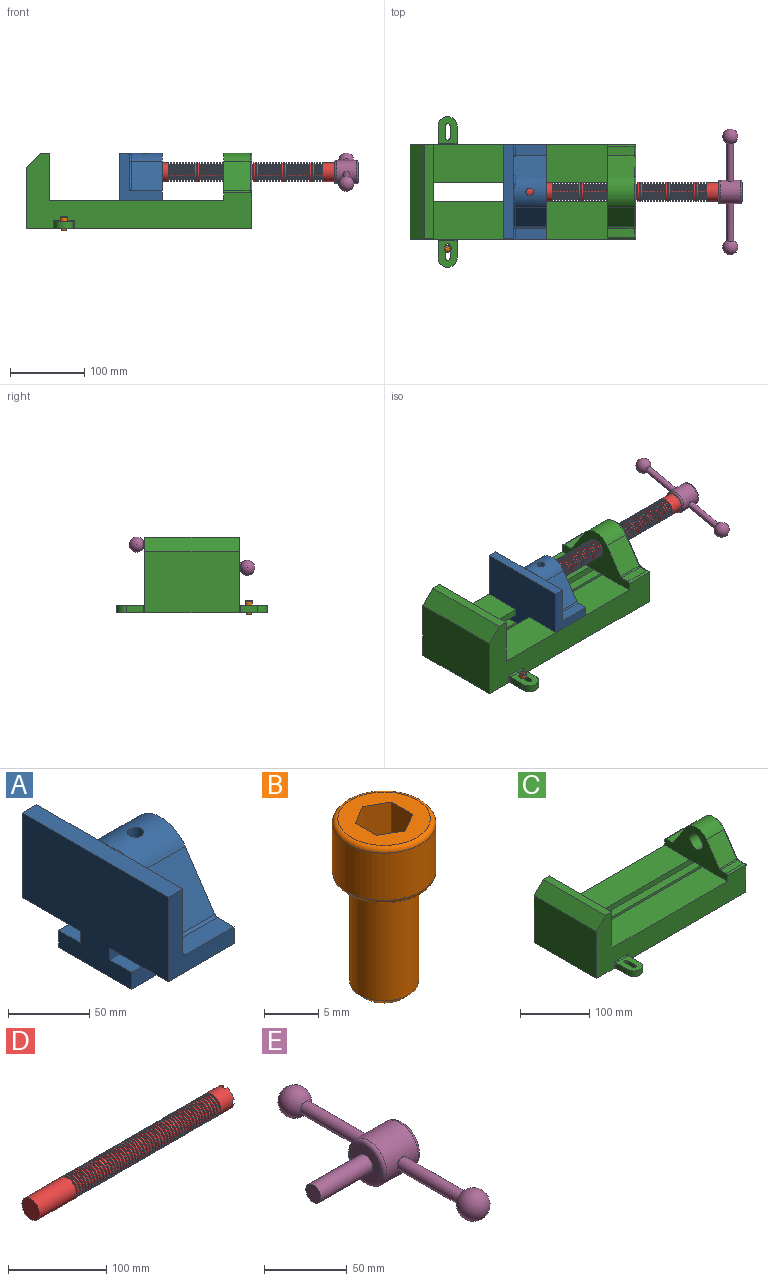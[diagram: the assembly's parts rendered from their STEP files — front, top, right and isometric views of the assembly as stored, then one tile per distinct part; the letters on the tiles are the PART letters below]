
ASSEMBLY  parts=5 mates=5
PART A: 36 faces, bbox 57.2x127x89 mm
  f0: plane 57.15x50.8mm, normal (0,0,-1), area 2903.2mm2, adj f6,f9,f10,f23
  f1: cylinder r=12.7mm len=44.45mm, axis (1,0,0), area 3464.3mm2, adj f6,f15,f16
  f2: plane 41.91x14.52mm, normal (0,0,1), area 608.5mm2, adj f6,f11,f24,f25
  f3: plane 51.86x48.26mm, normal (1,0,0), area 1495.7mm2, adj f8,f10,f31,f33,f35
  f4: plane 51.86x48.26mm, normal (1,0,0), area 1495.7mm2, adj f8,f11,f24,f28,f29
  f5: plane 57.15x50.8mm, normal (0,0,-1), area 2903.2mm2, adj f6,f9,f11,f22
  f6: plane 127x85.09mm, normal (1,0,0), area 5190.6mm2, adj f0,f1,f2,f5,f7,f10,f11,f12
  f7: plane 41.91x14.52mm, normal (0,0,1), area 608.5mm2, adj f6,f10,f30,f31
  f8: plane 127x12.7mm, normal (0,0,1), area 1612.9mm2, adj f3,f4,f9,f10,f11,f26,f34
  f9: plane 127x85.09mm, normal (-1,0,0), area 9096.8mm2, adj f0,f5,f8,f10,f11,f17,f18,f19
  f10: plane 63.5x57.15mm, normal (0,-1,0), area 1372.3mm2, adj f0,f3,f6,f7,f8,f9,f31
  f11: plane 63.5x57.15mm, normal (0,1,0), area 1372.3mm2, adj f2,f4,f5,f6,f8,f9,f24
  f12: plane 41.91x38.43mm, normal (0,-0.83,0.56), area 1939.2mm2, adj f6,f13,f30,f33
  f13: cylinder r=25.4mm len=44.45mm, axis (1,0,0), area 2026.5mm2, adj f6,f12,f14,f16,f26,f28,f34,f35
  f14: plane 41.91x38.43mm, normal (0,0.83,0.56), area 1939.2mm2, adj f6,f13,f25,f29
  f15: plane 25.4x25.4mm, normal (1,0,0), area 506.7mm2, adj f1
  f16: cylinder r=5.08mm len=13.76mm, axis (0,0,1), area 414mm2, adj f1,f13
  f17: plane 57.15x19.05mm, normal (0,0,1), area 1088.7mm2, adj f6,f9,f18,f23
  f18: plane 57.15x12.7mm, normal (0,-1,0), area 725.8mm2, adj f6,f9,f17,f19
  f19: plane 63.5x57.15mm, normal (0,0,-1), area 3629mm2, adj f6,f9,f18,f20
  f20: plane 57.15x12.7mm, normal (0,1,0), area 725.8mm2, adj f6,f9,f19,f21
  f21: plane 57.15x19.05mm, normal (0,0,1), area 1088.7mm2, adj f6,f9,f20,f22
  f22: plane 57.15x8.89mm, normal (0,1,0), area 508.1mm2, adj f5,f6,f9,f21
  f23: plane 57.15x8.89mm, normal (0,-1,0), area 508.1mm2, adj f0,f6,f9,f17
  f24: cylinder r=2.54mm len=14.52mm, axis (0,-1,0), area 57.9mm2, adj f2,f4,f11,f27
  f25: cylinder r=2.54mm len=41.91mm, axis (1,0,0), area 104.3mm2, adj f2,f6,f14,f27
  f26: bspline ~12.24x2.8mm, area 20.9mm2, adj f8,f13,f28
  f27: sphere r=2.54mm, area 6.3mm2, adj f24,f25,f29
  f28: torus R=27.94mm, axis (1,0,0), area 57.8mm2, adj f4,f13,f26,f29
  f29: cylinder r=2.54mm len=39.84mm, axis (0,-0.56,0.83), area 184.6mm2, adj f4,f14,f27,f28
  f30: cylinder r=2.54mm len=41.91mm, axis (1,0,0), area 104.3mm2, adj f6,f7,f12,f32
  f31: cylinder r=2.54mm len=14.52mm, axis (0,-1,0), area 57.9mm2, adj f3,f7,f10,f32
  f32: sphere r=2.54mm, area 6.3mm2, adj f30,f31,f33
  f33: cylinder r=2.54mm len=39.84mm, axis (0,-0.56,-0.83), area 184.6mm2, adj f3,f12,f32,f35
  f34: bspline ~12.24x2.8mm, area 20.9mm2, adj f8,f13,f35
  f35: torus R=27.94mm, axis (1,0,0), area 57.8mm2, adj f3,f13,f33,f34
PART B: 15 faces, bbox 10.3x10.3x19.1 mm
  f0: plane 8.51x8.51mm, normal (0,0,1), area 37.2mm2, adj f5,f6,f7,f8,f9,f10,f14
  f1: cylinder r=3.17mm len=11.94mm, axis (0,0,1), area 238.2mm2, adj f4,f12
  f2: plane 4.83x4.83mm, normal (0,0,-1), area 18.3mm2, adj f12
  f3: cylinder r=4.76mm len=9.53mm, axis (0,0,-1), area 159.6mm2, adj f13,f14
  f4: plane 8.51x8.51mm, normal (0,0,-1), area 25.2mm2, adj f1,f13
  f5: plane 4.83x2.38mm, normal (-0.5,-0.87,0), area 13.3mm2, adj f0,f6,f10,f11
  f6: plane 4.83x2.38mm, normal (0.5,-0.87,0), area 13.3mm2, adj f0,f5,f7,f11
  f7: plane 4.83x2.75mm, normal (1,0,0), area 13.3mm2, adj f0,f6,f8,f11
  f8: plane 4.83x2.38mm, normal (0.5,0.87,0), area 13.3mm2, adj f0,f7,f9,f11
  f9: plane 4.83x2.38mm, normal (-0.5,0.87,0), area 13.3mm2, adj f0,f8,f10,f11
  f10: plane 4.83x2.75mm, normal (-1,0,0), area 13.3mm2, adj f0,f5,f9,f11
  f11: plane 5.5x4.76mm, normal (0,0,1), area 19.6mm2, adj f5,f6,f7,f8,f9,f10
  f12: cone r=3.17mm half-angle=45deg, axis (0,0,1), area 18.9mm2, adj f1,f2
  f13: torus R=4.25mm, axis (0,0,1), area 23mm2, adj f3,f4
  f14: torus R=4.25mm, axis (0,0,1), area 23mm2, adj f0,f3
PART C: 61 faces, bbox 304.8x203.2x103.7 mm
  f0: plane 304.8x101.6mm, normal (0,1,0), area 13520.3mm2, adj f3,f4,f5,f6,f7,f8,f9,f16
  f1: plane 304.8x101.6mm, normal (0,-1,0), area 13520.3mm2, adj f2,f3,f5,f6,f7,f8,f9,f16
  f2: plane 234.95x50.8mm, normal (0,0,1), area 11935.5mm2, adj f1,f5,f16,f26
  f3: plane 127x99.06mm, normal (1,0,0), area 7097.5mm2, adj f0,f1,f9,f14,f17,f18,f19,f20
  f4: plane 234.95x50.8mm, normal (0,0,1), area 11935.5mm2, adj f0,f5,f16,f27
  f5: plane 127x101.6mm, normal (1,0,0), area 9516.1mm2, adj f0,f1,f2,f4,f6,f9,f18,f19
  f6: plane 127x12.7mm, normal (0,0,1), area 1612.9mm2, adj f0,f1,f5,f7
  f7: plane 127x19.05mm, normal (-0.71,0,0.71), area 3421.5mm2, adj f0,f1,f6,f8
  f8: plane 127x82.55mm, normal (-1,0,0), area 10483.8mm2, adj f0,f1,f7,f9
  f9: plane 304.8x203.2mm, normal (0,0,-1), area 33298.3mm2, adj f0,f1,f3,f5,f8,f21,f22,f39
  f10: plane 35.56x11.98mm, normal (0,0,1), area 426mm2, adj f16,f28,f29,f30
  f11: plane 38.43x35.56mm, normal (0,0.83,0.56), area 1645.4mm2, adj f12,f16,f29,f32
  f12: cylinder r=25.4mm len=42.19mm, axis (1,0,0), area 1770.2mm2, adj f11,f13,f16,f33
  f13: plane 38.43x35.56mm, normal (0,-0.83,0.56), area 1645.4mm2, adj f12,f16,f34,f35
  f14: cylinder r=12.7mm len=38.1mm, axis (1,0,0), area 3040.2mm2, adj f3,f16
  f15: plane 35.56x11.98mm, normal (0,0,1), area 426mm2, adj f16,f34,f36,f38
  f16: plane 127x63.5mm, normal (-1,0,0), area 4155.5mm2, adj f0,f1,f2,f4,f10,f11,f12,f13
  f17: plane 38.1x25.4mm, normal (0,0,-1), area 967.7mm2, adj f3,f16,f26,f27
  f18: plane 273.05x19.05mm, normal (0,0,-1), area 5201.6mm2, adj f3,f5,f19,f26
  f19: plane 273.05x12.7mm, normal (0,1,0), area 3467.7mm2, adj f3,f5,f18,f20
  f20: plane 273.05x19.05mm, normal (0,0,1), area 5201.6mm2, adj f3,f5,f19,f21
  f21: plane 273.05x16.51mm, normal (0,1,0), area 4508.1mm2, adj f3,f5,f9,f20
  f22: plane 273.05x16.51mm, normal (0,-1,0), area 4508.1mm2, adj f3,f5,f9,f23
  f23: plane 273.05x19.05mm, normal (0,0,1), area 5201.6mm2, adj f3,f5,f22,f24
  f24: plane 273.05x12.7mm, normal (0,-1,0), area 3467.7mm2, adj f3,f5,f23,f25
  f25: plane 273.05x19.05mm, normal (0,0,-1), area 5201.6mm2, adj f3,f5,f24,f27
  f26: plane 273.05x8.89mm, normal (0,1,0), area 2427.4mm2, adj f2,f3,f5,f17,f18
  f27: plane 273.05x8.89mm, normal (0,-1,0), area 2427.4mm2, adj f3,f4,f5,f17,f25
  f28: cylinder r=2.54mm len=38.1mm, axis (1,0,0), area 148.3mm2, adj f0,f10,f16,f30
  f29: cylinder r=2.54mm len=35.56mm, axis (-1,0,0), area 88.5mm2, adj f10,f11,f16,f31
  f30: cylinder r=2.54mm len=14.52mm, axis (0,1,0), area 54.3mm2, adj f3,f10,f28,f31
  f31: torus R=5.08mm, axis (-1,0,0), area 13.5mm2, adj f3,f29,f30,f32
  f32: cylinder r=2.54mm len=39.84mm, axis (0,0.56,-0.83), area 184.6mm2, adj f3,f11,f31,f33
  f33: torus R=22.86mm, axis (-1,0,0), area 191.4mm2, adj f3,f12,f32,f35
  f34: cylinder r=2.54mm len=35.56mm, axis (-1,0,0), area 88.5mm2, adj f13,f15,f16,f37
  f35: cylinder r=2.54mm len=39.84mm, axis (0,0.56,0.83), area 184.6mm2, adj f3,f13,f33,f37
  f36: cylinder r=2.54mm len=38.1mm, axis (-1,0,0), area 148.3mm2, adj f1,f15,f16,f38
  f37: torus R=5.08mm, axis (-1,0,0), area 13.5mm2, adj f3,f34,f35,f38
  f38: cylinder r=2.54mm len=14.52mm, axis (0,1,0), area 54.3mm2, adj f3,f15,f36,f37
  f39: plane 23.88x9.53mm, normal (-1,0,0), area 227.4mm2, adj f9,f45,f46,f60
  f40: plane 23.88x9.53mm, normal (1,0,0), area 227.4mm2, adj f9,f45,f46,f58
  f41: cylinder r=3.3mm len=9.53mm, axis (0,0,-1), area 98.8mm2, adj f9,f42,f44,f46
  f42: plane 15.62x9.53mm, normal (-1,0,0), area 148.8mm2, adj f9,f41,f43,f46
  f43: cylinder r=3.3mm len=9.53mm, axis (0,0,-1), area 98.8mm2, adj f9,f42,f44,f46
  f44: plane 15.62x9.53mm, normal (1,0,0), area 148.8mm2, adj f9,f41,f43,f46
  f45: cylinder r=12.7mm len=25.4mm, axis (0,0,-1), area 380mm2, adj f9,f39,f40,f46
  f46: plane 36.58x25.4mm, normal (0,0,1), area 722.4mm2, adj f39,f40,f41,f42,f43,f44,f45,f59
  f47: plane 23.88x9.53mm, normal (-1,0,0), area 227.4mm2, adj f9,f53,f54,f56
  f48: plane 23.88x9.53mm, normal (1,0,0), area 227.4mm2, adj f9,f53,f54,f55
  f49: cylinder r=3.3mm len=9.53mm, axis (0,0,-1), area 98.8mm2, adj f9,f50,f52,f54
  f50: plane 15.62x9.53mm, normal (-1,0,0), area 148.8mm2, adj f9,f49,f51,f54
  f51: cylinder r=3.3mm len=9.53mm, axis (0,0,-1), area 98.8mm2, adj f9,f50,f52,f54
  f52: plane 15.62x9.53mm, normal (1,0,0), area 148.8mm2, adj f9,f49,f51,f54
  f53: cylinder r=12.7mm len=25.4mm, axis (0,0,-1), area 380mm2, adj f9,f47,f48,f54
  f54: plane 36.58x25.4mm, normal (0,0,1), area 722.4mm2, adj f47,f48,f49,f50,f51,f52,f53,f57
  f55: cylinder r=1.52mm len=11.05mm, axis (0,0,-1), area 24.1mm2, adj f0,f9,f48,f57
  f56: cylinder r=1.52mm len=11.05mm, axis (0,0,1), area 24.1mm2, adj f0,f9,f47,f57
  f57: cylinder r=1.52mm len=28.45mm, axis (1,0,0), area 63.5mm2, adj f0,f54,f55,f56
  f58: cylinder r=1.52mm len=11.05mm, axis (0,0,1), area 24.1mm2, adj f1,f9,f40,f59
  f59: cylinder r=1.52mm len=28.45mm, axis (-1,0,0), area 63.5mm2, adj f1,f46,f58,f60
  f60: cylinder r=1.52mm len=11.05mm, axis (0,0,-1), area 24.1mm2, adj f1,f9,f39,f59
PART D: 220 faces, bbox 279.4x25.4x25.4 mm
  f0: cylinder r=12.7mm len=25.4mm, axis (-1,0,0), area 1468.2mm2, adj f1,f2,f3,f5,f7,f208,f209,f210
  f1: plane 9.9x9.9mm, normal (1,0,0), area 62.3mm2, adj f0,f4,f213,f216
  f2: plane 9.9x9.9mm, normal (1,0,0), area 62.3mm2, adj f0,f4,f210,f218
  f3: plane 9.9x9.9mm, normal (1,0,0), area 62.3mm2, adj f0,f4,f209,f212
  f4: cylinder r=6.35mm len=25.4mm, axis (1,0,0), area 960.3mm2, adj f1,f2,f3,f5,f6,f208,f209,f210
  f5: plane 9.9x9.9mm, normal (1,0,0), area 62.3mm2, adj f0,f4,f215,f217
  f6: plane 12.7x12.7mm, normal (1,0,0), area 126.7mm2, adj f4
  f7: cone r=12.7mm half-angle=76deg, axis (1,0,0), area 188mm2, adj f0,f9
  f8: cone r=10.16mm half-angle=76deg, axis (-1,0,0), area 188mm2, adj f9,f10
  f9: cylinder r=10.16mm len=20.32mm, axis (1,0,0), area 81.1mm2, adj f7,f8
  f10: cylinder r=12.7mm len=25.4mm, axis (-1,0,0), area 131.7mm2, adj f8,f11
  f11: cone r=12.7mm half-angle=76deg, axis (1,0,0), area 188mm2, adj f10,f13
  f12: cone r=10.16mm half-angle=76deg, axis (-1,0,0), area 188mm2, adj f13,f14
  f13: cylinder r=10.16mm len=20.32mm, axis (1,0,0), area 81.1mm2, adj f11,f12
  f14: cylinder r=12.7mm len=25.4mm, axis (-1,0,0), area 131.7mm2, adj f12,f15
  f15: cone r=12.7mm half-angle=76deg, axis (1,0,0), area 188mm2, adj f14,f17
  f16: cone r=10.16mm half-angle=76deg, axis (-1,0,0), area 188mm2, adj f17,f18
  f17: cylinder r=10.16mm len=20.32mm, axis (1,0,0), area 81.1mm2, adj f15,f16
  f18: cylinder r=12.7mm len=25.4mm, axis (-1,0,0), area 131.7mm2, adj f16,f19
  f19: cone r=12.7mm half-angle=76deg, axis (1,0,0), area 188mm2, adj f18,f21
  f20: cone r=10.16mm half-angle=76deg, axis (-1,0,0), area 188mm2, adj f21,f22
  f21: cylinder r=10.16mm len=20.32mm, axis (1,0,0), area 81.1mm2, adj f19,f20
  f22: cylinder r=12.7mm len=25.4mm, axis (-1,0,0), area 131.7mm2, adj f20,f23
  f23: cone r=12.7mm half-angle=76deg, axis (1,0,0), area 188mm2, adj f22,f25
  f24: cone r=10.16mm half-angle=76deg, axis (-1,0,0), area 188mm2, adj f25,f26
  f25: cylinder r=10.16mm len=20.32mm, axis (1,0,0), area 81.1mm2, adj f23,f24
  f26: cylinder r=12.7mm len=25.4mm, axis (-1,0,0), area 131.7mm2, adj f24,f27
  f27: cone r=12.7mm half-angle=76deg, axis (1,0,0), area 188mm2, adj f26,f29
  f28: cone r=10.16mm half-angle=76deg, axis (-1,0,0), area 188mm2, adj f29,f30
  f29: cylinder r=10.16mm len=20.32mm, axis (1,0,0), area 81.1mm2, adj f27,f28
  f30: cylinder r=12.7mm len=25.4mm, axis (-1,0,0), area 131.7mm2, adj f28,f31
  f31: cone r=12.7mm half-angle=76deg, axis (1,0,0), area 188mm2, adj f30,f33
  f32: cone r=10.16mm half-angle=76deg, axis (-1,0,0), area 188mm2, adj f33,f34
  f33: cylinder r=10.16mm len=20.32mm, axis (1,0,0), area 81.1mm2, adj f31,f32
  f34: cylinder r=12.7mm len=25.4mm, axis (-1,0,0), area 131.7mm2, adj f32,f35
  f35: cone r=12.7mm half-angle=76deg, axis (1,0,0), area 188mm2, adj f34,f37
  f36: cone r=10.16mm half-angle=76deg, axis (-1,0,0), area 188mm2, adj f37,f38
  f37: cylinder r=10.16mm len=20.32mm, axis (1,0,0), area 81.1mm2, adj f35,f36
  f38: cylinder r=12.7mm len=25.4mm, axis (-1,0,0), area 131.7mm2, adj f36,f39
  f39: cone r=12.7mm half-angle=76deg, axis (1,0,0), area 188mm2, adj f38,f41
  f40: cone r=10.16mm half-angle=76deg, axis (-1,0,0), area 188mm2, adj f41,f42
  f41: cylinder r=10.16mm len=20.32mm, axis (1,0,0), area 81.1mm2, adj f39,f40
  f42: cylinder r=12.7mm len=25.4mm, axis (-1,0,0), area 131.7mm2, adj f40,f43
  f43: cone r=12.7mm half-angle=76deg, axis (1,0,0), area 188mm2, adj f42,f45
  f44: cone r=10.16mm half-angle=76deg, axis (-1,0,0), area 188mm2, adj f45,f46
  f45: cylinder r=10.16mm len=20.32mm, axis (1,0,0), area 81.1mm2, adj f43,f44
  f46: cylinder r=12.7mm len=25.4mm, axis (-1,0,0), area 131.7mm2, adj f44,f47
  f47: cone r=12.7mm half-angle=76deg, axis (1,0,0), area 188mm2, adj f46,f49
  f48: cone r=10.16mm half-angle=76deg, axis (-1,0,0), area 188mm2, adj f49,f50
  f49: cylinder r=10.16mm len=20.32mm, axis (1,0,0), area 81.1mm2, adj f47,f48
  f50: cylinder r=12.7mm len=25.4mm, axis (-1,0,0), area 131.7mm2, adj f48,f51
  f51: cone r=12.7mm half-angle=76deg, axis (1,0,0), area 188mm2, adj f50,f53
  f52: cone r=10.16mm half-angle=76deg, axis (-1,0,0), area 188mm2, adj f53,f54
  f53: cylinder r=10.16mm len=20.32mm, axis (1,0,0), area 81.1mm2, adj f51,f52
  f54: cylinder r=12.7mm len=25.4mm, axis (-1,0,0), area 131.7mm2, adj f52,f55
  f55: cone r=12.7mm half-angle=76deg, axis (1,0,0), area 188mm2, adj f54,f57
  f56: cone r=10.16mm half-angle=76deg, axis (-1,0,0), area 188mm2, adj f57,f58
  f57: cylinder r=10.16mm len=20.32mm, axis (1,0,0), area 81.1mm2, adj f55,f56
  f58: cylinder r=12.7mm len=25.4mm, axis (-1,0,0), area 131.7mm2, adj f56,f59
  f59: cone r=12.7mm half-angle=76deg, axis (1,0,0), area 188mm2, adj f58,f61
  f60: cone r=10.16mm half-angle=76deg, axis (-1,0,0), area 188mm2, adj f61,f62
  f61: cylinder r=10.16mm len=20.32mm, axis (1,0,0), area 81.1mm2, adj f59,f60
  f62: cylinder r=12.7mm len=25.4mm, axis (-1,0,0), area 131.7mm2, adj f60,f63
  f63: cone r=12.7mm half-angle=76deg, axis (1,0,0), area 188mm2, adj f62,f65
  f64: cone r=10.16mm half-angle=76deg, axis (-1,0,0), area 188mm2, adj f65,f66
  f65: cylinder r=10.16mm len=20.32mm, axis (1,0,0), area 81.1mm2, adj f63,f64
  f66: cylinder r=12.7mm len=25.4mm, axis (-1,0,0), area 131.7mm2, adj f64,f67
  f67: cone r=12.7mm half-angle=76deg, axis (1,0,0), area 188mm2, adj f66,f69
  f68: cone r=10.16mm half-angle=76deg, axis (-1,0,0), area 188mm2, adj f69,f70
  f69: cylinder r=10.16mm len=20.32mm, axis (1,0,0), area 81.1mm2, adj f67,f68
  f70: cylinder r=12.7mm len=25.4mm, axis (-1,0,0), area 131.7mm2, adj f68,f71
  f71: cone r=12.7mm half-angle=76deg, axis (1,0,0), area 188mm2, adj f70,f73
  f72: cone r=10.16mm half-angle=76deg, axis (-1,0,0), area 188mm2, adj f73,f74
  f73: cylinder r=10.16mm len=20.32mm, axis (1,0,0), area 81.1mm2, adj f71,f72
  f74: cylinder r=12.7mm len=25.4mm, axis (-1,0,0), area 131.7mm2, adj f72,f75
  f75: cone r=12.7mm half-angle=76deg, axis (1,0,0), area 188mm2, adj f74,f77
  f76: cone r=10.16mm half-angle=76deg, axis (-1,0,0), area 188mm2, adj f77,f78
  f77: cylinder r=10.16mm len=20.32mm, axis (1,0,0), area 81.1mm2, adj f75,f76
  f78: cylinder r=12.7mm len=25.4mm, axis (-1,0,0), area 131.7mm2, adj f76,f79
  f79: cone r=12.7mm half-angle=76deg, axis (1,0,0), area 188mm2, adj f78,f81
  f80: cone r=10.16mm half-angle=76deg, axis (-1,0,0), area 188mm2, adj f81,f82
  f81: cylinder r=10.16mm len=20.32mm, axis (1,0,0), area 81.1mm2, adj f79,f80
  f82: cylinder r=12.7mm len=25.4mm, axis (-1,0,0), area 131.7mm2, adj f80,f83
  f83: cone r=12.7mm half-angle=76deg, axis (1,0,0), area 188mm2, adj f82,f85
  f84: cone r=10.16mm half-angle=76deg, axis (-1,0,0), area 188mm2, adj f85,f86
  f85: cylinder r=10.16mm len=20.32mm, axis (1,0,0), area 81.1mm2, adj f83,f84
  f86: cylinder r=12.7mm len=25.4mm, axis (-1,0,0), area 131.7mm2, adj f84,f87
  f87: cone r=12.7mm half-angle=76deg, axis (1,0,0), area 188mm2, adj f86,f89
  f88: cone r=10.16mm half-angle=76deg, axis (-1,0,0), area 188mm2, adj f89,f90
  f89: cylinder r=10.16mm len=20.32mm, axis (1,0,0), area 81.1mm2, adj f87,f88
  f90: cylinder r=12.7mm len=25.4mm, axis (-1,0,0), area 131.7mm2, adj f88,f91
  f91: cone r=12.7mm half-angle=76deg, axis (1,0,0), area 188mm2, adj f90,f93
  f92: cone r=10.16mm half-angle=76deg, axis (-1,0,0), area 188mm2, adj f93,f94
  f93: cylinder r=10.16mm len=20.32mm, axis (1,0,0), area 81.1mm2, adj f91,f92
  f94: cylinder r=12.7mm len=25.4mm, axis (-1,0,0), area 131.7mm2, adj f92,f95
  f95: cone r=12.7mm half-angle=76deg, axis (1,0,0), area 188mm2, adj f94,f97
  f96: cone r=10.16mm half-angle=76deg, axis (-1,0,0), area 188mm2, adj f97,f98
  f97: cylinder r=10.16mm len=20.32mm, axis (1,0,0), area 81.1mm2, adj f95,f96
  f98: cylinder r=12.7mm len=25.4mm, axis (-1,0,0), area 131.7mm2, adj f96,f99
  f99: cone r=12.7mm half-angle=76deg, axis (1,0,0), area 188mm2, adj f98,f101
  f100: cone r=10.16mm half-angle=76deg, axis (-1,0,0), area 188mm2, adj f101,f102
  f101: cylinder r=10.16mm len=20.32mm, axis (1,0,0), area 81.1mm2, adj f99,f100
  f102: cylinder r=12.7mm len=25.4mm, axis (-1,0,0), area 131.7mm2, adj f100,f103
  f103: cone r=12.7mm half-angle=76deg, axis (1,0,0), area 188mm2, adj f102,f105
  f104: cone r=10.16mm half-angle=76deg, axis (-1,0,0), area 188mm2, adj f105,f106
  f105: cylinder r=10.16mm len=20.32mm, axis (1,0,0), area 81.1mm2, adj f103,f104
  f106: cylinder r=12.7mm len=25.4mm, axis (-1,0,0), area 131.7mm2, adj f104,f107
  f107: cone r=12.7mm half-angle=76deg, axis (1,0,0), area 188mm2, adj f106,f109
  f108: cone r=10.16mm half-angle=76deg, axis (-1,0,0), area 188mm2, adj f109,f110
  f109: cylinder r=10.16mm len=20.32mm, axis (1,0,0), area 81.1mm2, adj f107,f108
  f110: cylinder r=12.7mm len=25.4mm, axis (-1,0,0), area 131.7mm2, adj f108,f111
  f111: cone r=12.7mm half-angle=76deg, axis (1,0,0), area 188mm2, adj f110,f113
  f112: cone r=10.16mm half-angle=76deg, axis (-1,0,0), area 188mm2, adj f113,f114
  f113: cylinder r=10.16mm len=20.32mm, axis (1,0,0), area 81.1mm2, adj f111,f112
  f114: cylinder r=12.7mm len=25.4mm, axis (-1,0,0), area 131.7mm2, adj f112,f115
  f115: cone r=12.7mm half-angle=76deg, axis (1,0,0), area 188mm2, adj f114,f117
  f116: cone r=10.16mm half-angle=76deg, axis (-1,0,0), area 188mm2, adj f117,f118
  f117: cylinder r=10.16mm len=20.32mm, axis (1,0,0), area 81.1mm2, adj f115,f116
  f118: cylinder r=12.7mm len=25.4mm, axis (-1,0,0), area 131.7mm2, adj f116,f119
  f119: cone r=12.7mm half-angle=76deg, axis (1,0,0), area 188mm2, adj f118,f121
  f120: cone r=10.16mm half-angle=76deg, axis (-1,0,0), area 188mm2, adj f121,f122
  f121: cylinder r=10.16mm len=20.32mm, axis (1,0,0), area 81.1mm2, adj f119,f120
  f122: cylinder r=12.7mm len=25.4mm, axis (-1,0,0), area 131.7mm2, adj f120,f123
  f123: cone r=12.7mm half-angle=76deg, axis (1,0,0), area 188mm2, adj f122,f125
  f124: cone r=10.16mm half-angle=76deg, axis (-1,0,0), area 188mm2, adj f125,f126
  f125: cylinder r=10.16mm len=20.32mm, axis (1,0,0), area 81.1mm2, adj f123,f124
  f126: cylinder r=12.7mm len=25.4mm, axis (-1,0,0), area 131.7mm2, adj f124,f127
  f127: cone r=12.7mm half-angle=76deg, axis (1,0,0), area 188mm2, adj f126,f129
  f128: cone r=10.16mm half-angle=76deg, axis (-1,0,0), area 188mm2, adj f129,f130
  f129: cylinder r=10.16mm len=20.32mm, axis (1,0,0), area 81.1mm2, adj f127,f128
  f130: cylinder r=12.7mm len=25.4mm, axis (-1,0,0), area 131.7mm2, adj f128,f131
  f131: cone r=12.7mm half-angle=76deg, axis (1,0,0), area 188mm2, adj f130,f133
  f132: cone r=10.16mm half-angle=76deg, axis (-1,0,0), area 188mm2, adj f133,f134
  f133: cylinder r=10.16mm len=20.32mm, axis (1,0,0), area 81.1mm2, adj f131,f132
  f134: cylinder r=12.7mm len=25.4mm, axis (-1,0,0), area 131.7mm2, adj f132,f135
  f135: cone r=12.7mm half-angle=76deg, axis (1,0,0), area 188mm2, adj f134,f137
  f136: cone r=10.16mm half-angle=76deg, axis (-1,0,0), area 188mm2, adj f137,f138
  f137: cylinder r=10.16mm len=20.32mm, axis (1,0,0), area 81.1mm2, adj f135,f136
  f138: cylinder r=12.7mm len=25.4mm, axis (-1,0,0), area 131.7mm2, adj f136,f139
  f139: cone r=12.7mm half-angle=76deg, axis (1,0,0), area 188mm2, adj f138,f141
  f140: cone r=10.16mm half-angle=76deg, axis (-1,0,0), area 188mm2, adj f141,f142
  f141: cylinder r=10.16mm len=20.32mm, axis (1,0,0), area 81.1mm2, adj f139,f140
  f142: cylinder r=12.7mm len=25.4mm, axis (-1,0,0), area 131.7mm2, adj f140,f143
  f143: cone r=12.7mm half-angle=76deg, axis (1,0,0), area 188mm2, adj f142,f145
  f144: cone r=10.16mm half-angle=76deg, axis (-1,0,0), area 188mm2, adj f145,f146
  f145: cylinder r=10.16mm len=20.32mm, axis (1,0,0), area 81.1mm2, adj f143,f144
  f146: cylinder r=12.7mm len=25.4mm, axis (-1,0,0), area 131.7mm2, adj f144,f147
  f147: cone r=12.7mm half-angle=76deg, axis (1,0,0), area 188mm2, adj f146,f149
  f148: cone r=10.16mm half-angle=76deg, axis (-1,0,0), area 188mm2, adj f149,f150
  f149: cylinder r=10.16mm len=20.32mm, axis (1,0,0), area 81.1mm2, adj f147,f148
  f150: cylinder r=12.7mm len=25.4mm, axis (-1,0,0), area 131.7mm2, adj f148,f151
  f151: cone r=12.7mm half-angle=76deg, axis (1,0,0), area 188mm2, adj f150,f153
  f152: cone r=10.16mm half-angle=76deg, axis (-1,0,0), area 188mm2, adj f153,f154
  f153: cylinder r=10.16mm len=20.32mm, axis (1,0,0), area 81.1mm2, adj f151,f152
  f154: cylinder r=12.7mm len=25.4mm, axis (-1,0,0), area 131.7mm2, adj f152,f155
  f155: cone r=12.7mm half-angle=76deg, axis (1,0,0), area 188mm2, adj f154,f157
  f156: cone r=10.16mm half-angle=76deg, axis (-1,0,0), area 188mm2, adj f157,f158
  f157: cylinder r=10.16mm len=20.32mm, axis (1,0,0), area 81.1mm2, adj f155,f156
  f158: cylinder r=12.7mm len=25.4mm, axis (-1,0,0), area 131.7mm2, adj f156,f159
  f159: cone r=12.7mm half-angle=76deg, axis (1,0,0), area 188mm2, adj f158,f161
  f160: cone r=10.16mm half-angle=76deg, axis (-1,0,0), area 188mm2, adj f161,f162
  f161: cylinder r=10.16mm len=20.32mm, axis (1,0,0), area 81.1mm2, adj f159,f160
  f162: cylinder r=12.7mm len=25.4mm, axis (-1,0,0), area 131.7mm2, adj f160,f163
  f163: cone r=12.7mm half-angle=76deg, axis (1,0,0), area 188mm2, adj f162,f165
  f164: cone r=10.16mm half-angle=76deg, axis (-1,0,0), area 188mm2, adj f165,f166
  f165: cylinder r=10.16mm len=20.32mm, axis (1,0,0), area 81.1mm2, adj f163,f164
  f166: cylinder r=12.7mm len=25.4mm, axis (-1,0,0), area 131.7mm2, adj f164,f167
  f167: cone r=12.7mm half-angle=76deg, axis (1,0,0), area 188mm2, adj f166,f169
  f168: cone r=10.16mm half-angle=76deg, axis (-1,0,0), area 188mm2, adj f169,f170
  f169: cylinder r=10.16mm len=20.32mm, axis (1,0,0), area 81.1mm2, adj f167,f168
  f170: cylinder r=12.7mm len=25.4mm, axis (-1,0,0), area 131.7mm2, adj f168,f171
  f171: cone r=12.7mm half-angle=76deg, axis (1,0,0), area 188mm2, adj f170,f173
  f172: cone r=10.16mm half-angle=76deg, axis (-1,0,0), area 188mm2, adj f173,f174
  f173: cylinder r=10.16mm len=20.32mm, axis (1,0,0), area 81.1mm2, adj f171,f172
  f174: cylinder r=12.7mm len=25.4mm, axis (-1,0,0), area 131.7mm2, adj f172,f175
  f175: cone r=12.7mm half-angle=76deg, axis (1,0,0), area 188mm2, adj f174,f177
  f176: cone r=10.16mm half-angle=76deg, axis (-1,0,0), area 188mm2, adj f177,f178
  f177: cylinder r=10.16mm len=20.32mm, axis (1,0,0), area 81.1mm2, adj f175,f176
  f178: cylinder r=12.7mm len=25.4mm, axis (-1,0,0), area 131.7mm2, adj f176,f179
  f179: cone r=12.7mm half-angle=76deg, axis (1,0,0), area 188mm2, adj f178,f181
  f180: cone r=10.16mm half-angle=76deg, axis (-1,0,0), area 188mm2, adj f181,f182
  f181: cylinder r=10.16mm len=20.32mm, axis (1,0,0), area 81.1mm2, adj f179,f180
  f182: cylinder r=12.7mm len=25.4mm, axis (-1,0,0), area 131.7mm2, adj f180,f183
  f183: cone r=12.7mm half-angle=76deg, axis (1,0,0), area 188mm2, adj f182,f185
  f184: cone r=10.16mm half-angle=76deg, axis (-1,0,0), area 188mm2, adj f185,f186
  f185: cylinder r=10.16mm len=20.32mm, axis (1,0,0), area 81.1mm2, adj f183,f184
  f186: cylinder r=12.7mm len=25.4mm, axis (-1,0,0), area 131.7mm2, adj f184,f187
  f187: cone r=12.7mm half-angle=76deg, axis (1,0,0), area 188mm2, adj f186,f189
  f188: cone r=10.16mm half-angle=76deg, axis (-1,0,0), area 188mm2, adj f189,f190
  f189: cylinder r=10.16mm len=20.32mm, axis (1,0,0), area 81.1mm2, adj f187,f188
  f190: cylinder r=12.7mm len=25.4mm, axis (-1,0,0), area 131.7mm2, adj f188,f191
  f191: cone r=12.7mm half-angle=76deg, axis (1,0,0), area 188mm2, adj f190,f193
  f192: cone r=10.16mm half-angle=76deg, axis (-1,0,0), area 188mm2, adj f193,f194
  f193: cylinder r=10.16mm len=20.32mm, axis (1,0,0), area 81.1mm2, adj f191,f192
  f194: cylinder r=12.7mm len=25.4mm, axis (-1,0,0), area 131.7mm2, adj f192,f195
  f195: cone r=12.7mm half-angle=76deg, axis (1,0,0), area 188mm2, adj f194,f197
  f196: cone r=10.16mm half-angle=76deg, axis (-1,0,0), area 188mm2, adj f197,f198
  f197: cylinder r=10.16mm len=20.32mm, axis (1,0,0), area 81.1mm2, adj f195,f196
  f198: cylinder r=12.7mm len=25.4mm, axis (-1,0,0), area 131.7mm2, adj f196,f199
  f199: cone r=12.7mm half-angle=76deg, axis (1,0,0), area 188mm2, adj f198,f201
  f200: cone r=10.16mm half-angle=76deg, axis (-1,0,0), area 188mm2, adj f201,f202
  f201: cylinder r=10.16mm len=20.32mm, axis (1,0,0), area 81.1mm2, adj f199,f200
  f202: cylinder r=12.7mm len=25.4mm, axis (-1,0,0), area 131.7mm2, adj f200,f203
  f203: cone r=12.7mm half-angle=76deg, axis (1,0,0), area 188mm2, adj f202,f205
  f204: cone r=10.16mm half-angle=76deg, axis (-1,0,0), area 188mm2, adj f205,f207
  f205: cylinder r=10.16mm len=20.32mm, axis (1,0,0), area 81.1mm2, adj f203,f204
  f206: plane 25.4x25.4mm, normal (-1,0,0), area 506.7mm2, adj f207
  f207: cylinder r=12.7mm len=52.45mm, axis (-1,0,0), area 4185.4mm2, adj f204,f206
  f208: plane 6.88x5.08mm, normal (1,0,0), area 32.7mm2, adj f0,f4,f209,f210
  f209: plane 6.62x2.54mm, normal (0,-1,0), area 16.8mm2, adj f0,f3,f4,f208
  f210: plane 6.62x2.54mm, normal (0,1,0), area 16.8mm2, adj f0,f2,f4,f208
  f211: plane 6.88x5.08mm, normal (1,0,0), area 32.7mm2, adj f0,f4,f212,f213
  f212: plane 6.62x2.54mm, normal (0,0,1), area 16.8mm2, adj f0,f3,f4,f211
  f213: plane 6.62x2.54mm, normal (0,0,-1), area 16.8mm2, adj f0,f1,f4,f211
  f214: plane 6.88x5.08mm, normal (1,0,0), area 32.7mm2, adj f0,f4,f215,f216
  f215: plane 6.62x2.54mm, normal (0,1,0), area 16.8mm2, adj f0,f4,f5,f214
  f216: plane 6.62x2.54mm, normal (0,-1,0), area 16.8mm2, adj f0,f1,f4,f214
  f217: plane 6.62x2.54mm, normal (0,0,-1), area 16.8mm2, adj f0,f4,f5,f219
  f218: plane 6.62x2.54mm, normal (0,0,1), area 16.8mm2, adj f0,f2,f4,f219
  f219: plane 6.88x5.08mm, normal (1,0,0), area 32.7mm2, adj f0,f4,f217,f218
PART E: 11 faces, bbox 76.2x172.7x34.4 mm
  f0: sphere r=10.16mm, area 1231.8mm2, adj f1
  f1: cylinder r=4.45mm len=51.82mm, axis (0,1,0), area 1438.5mm2, adj f0,f4
  f2: sphere r=10.16mm, area 1231.8mm2, adj f3
  f3: cylinder r=4.45mm len=51.82mm, axis (0,1,0), area 1438.5mm2, adj f2,f4
  f4: cylinder r=15.88mm len=31.75mm, axis (-1,0,0), area 2534.7mm2, adj f1,f3,f9,f10
  f5: cylinder r=6.35mm len=44.45mm, axis (-1,0,0), area 1773.5mm2, adj f6,f8
  f6: plane 12.7x12.7mm, normal (-1,0,0), area 126.7mm2, adj f5
  f7: plane 26.67x26.67mm, normal (1,0,0), area 558.6mm2, adj f10
  f8: plane 26.67x26.67mm, normal (-1,0,0), area 432mm2, adj f5,f9
  f9: torus R=13.33mm, axis (1,0,0), area 374.8mm2, adj f4,f8
  f10: torus R=13.33mm, axis (1,0,0), area 374.8mm2, adj f4,f7
PLACE A t=(94.83,0,0)mm
PLACE B rot(axis=(0,0,1),46.2deg) t=(-254,-76.56,9.52)mm
PLACE C at identity fixed
PLACE D rot(axis=(1,0,0),11.9deg) t=(94.83,15.66,1.63)mm
PLACE E rot(axis=(1,0,0),11.9deg) t=(73.24,15.66,1.63)mm
MATE fastened D.f4 <-> E.f5  axis (1,0,0) through (111.34,0,76.2)mm
MATE planar A.f0 <-> C.f2  axis (0,0,-1) through (-149.64,-38.1,38.1)mm
MATE pin_slot B.f1 <-> C.f41  axis (0,0,1) through (-254,-76.56,9.52)mm
MATE revolute D.f7 <-> A.f28  axis (-1,0,0) through (-165.52,0,76.2)mm
MATE cylindrical C.f12 <-> D.f7  axis (-1,0,0) through (-38.1,0,76.2)mm
